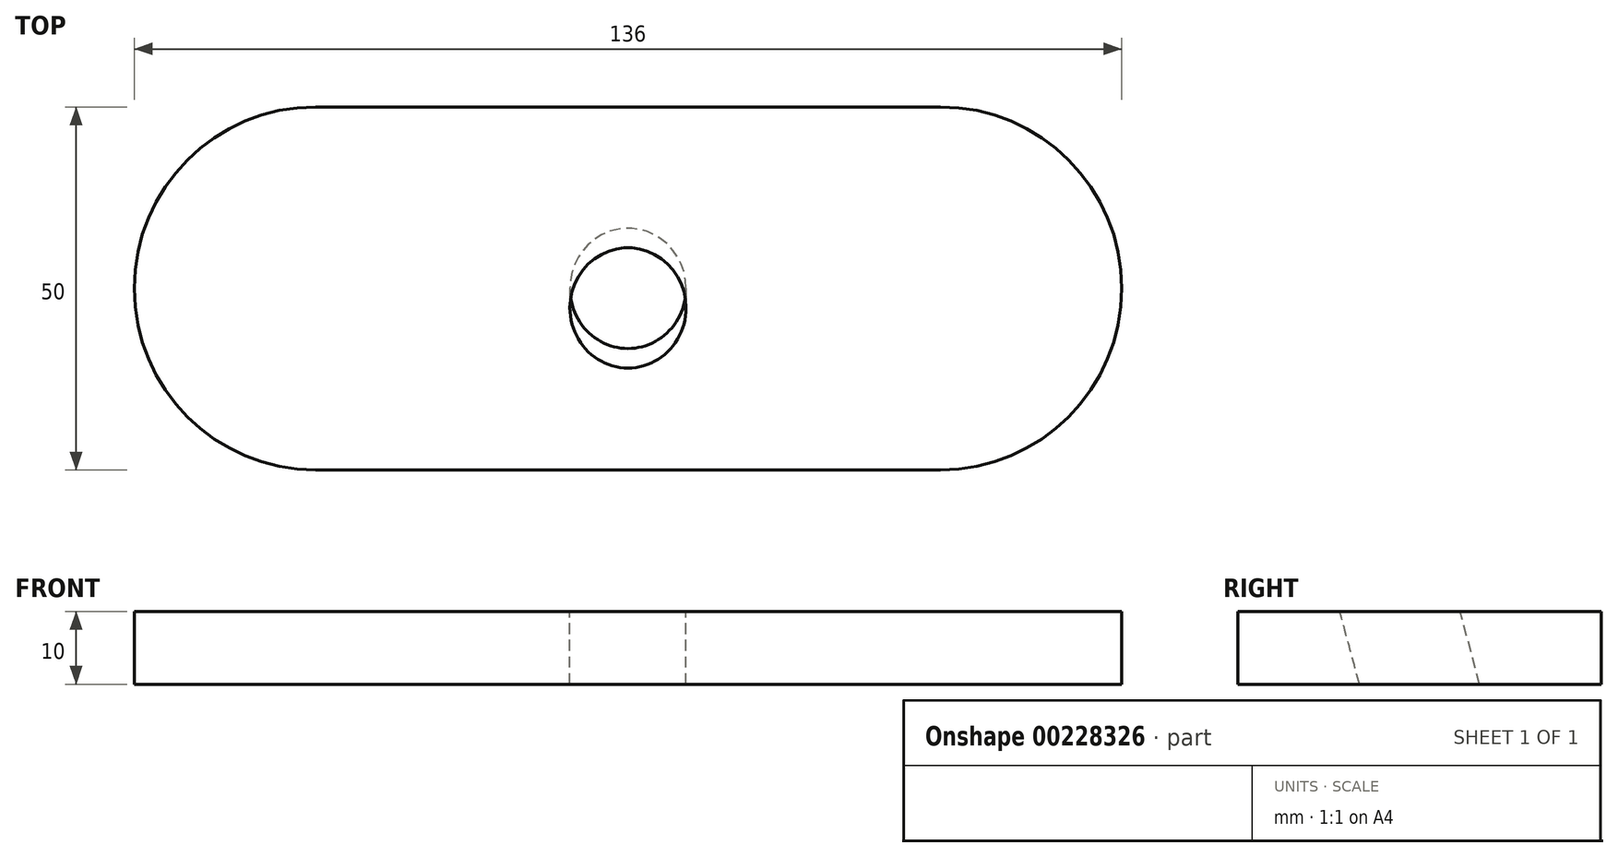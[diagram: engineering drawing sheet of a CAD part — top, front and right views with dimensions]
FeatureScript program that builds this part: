
annotation { "Feature Type Name" : "Feature", "Feature Type Description" : "" }
export const myFeature = defineFeature(function(context is Context, id is Id, definition is map)
    precondition{}
    {
        {
            var Q0;
            Q0=qCreatedBy(makeId("Top.planeOp"),FACE);
            var sketch = newSketch(context, id + "F0", { "sketchPlane" : qUnion([Q0])});
            skLineSegment(sketch, "E0", {"start": v(-43, 25) * mm, "end": v(43, 25) * mm});
            skLineSegment(sketch, "E1", {"start": v(-43, -25) * mm, "end": v(43, -25) * mm});
            skArc(sketch, "E2", {"start": v(-43, 25) * mm, "mid": v(-68, 0) * mm, "end": v(-43, -25) * mm});
            skArc(sketch, "E3", {"start": v(43, -25) * mm, "mid": v(68, 0) * mm, "end": v(43, 25) * mm});
            skLineSegment(sketch, "E4", {"start": v(0, 0) * mm, "end": v(-43, 25) * mm, "construction": true});
            skLineSegment(sketch, "E5", {"start": v(0, 0) * mm, "end": v(43, 25) * mm, "construction": true});
            skLineSegment(sketch, "E6", {"start": v(0, -25) * mm, "end": v(0, 25) * mm, "construction": true});
            skSolve(sketch);
        }
        {
            var Q0;
            Q0=makeQuery(id+"F0.imprint","IMPRINT",FACE,{"disambiguationData":[TD([[makeQuery(id+"F0.imprint","IMPRINT",EDGE,{"derivedFrom":sQuery(id+"F0.wireOp",EDGE,"E0")}),-1.0]])]});
            extrude(context, id + "F1", {"entities" : qUnion([Q0]), "depth" : 10 * mm});
        }
        {
            var Q0;
            Q0=makeQuery(id+"F1.opExtrude","CAP_EDGE",EDGE,{"disambiguationData":[OSD([sQuery(id+"F0.wireOp",EDGE,"E1")])],"isStart":false});
            cPlane(context, id + "F2", {"entities" : qUnion([Q0]), "cplaneType" : CPlaneType.LINE_ANGLE, "offset" : 25 * mm, "angle" : 285 * degree, "width" : 150 * mm, "height" : 150 * mm});
        }
        {
            var Q0;
            Q0=qCreatedBy(id+"F2.planeOp",FACE);
            var sketch = newSketch(context, id + "F3", { "sketchPlane" : qUnion([Q0])});
            skCircle(sketch, "E7", {"center": v(0, 0) * mm, "radius": 8 * mm});
            skSolve(sketch);
        }
        {
            var Q0;
            Q0=makeQuery(id+"F3.imprint","IMPRINT",FACE,{"disambiguationData":[TD([[makeQuery(id+"F3.imprint","IMPRINT",EDGE,{"derivedFrom":sQuery(id+"F3.wireOp",EDGE,"E7")}),1.0]])]});
            extrude(context, id + "F4", {"entities" : qUnion([Q0]), "operationType" : NewBodyOperationType.REMOVE, "depth" : 25 * mm});
        }
        {
            var Q0;
            Q0=sQuery(id+"F0.wireOp",EDGE,"E5");
            cPlane(context, id + "F5", {"entities" : qUnion([Q0]), "cplaneType" : CPlaneType.LINE_ANGLE, "offset" : 25 * mm, "angle" : 0 * degree, "width" : 150 * mm, "height" : 150 * mm});
        }
    });
